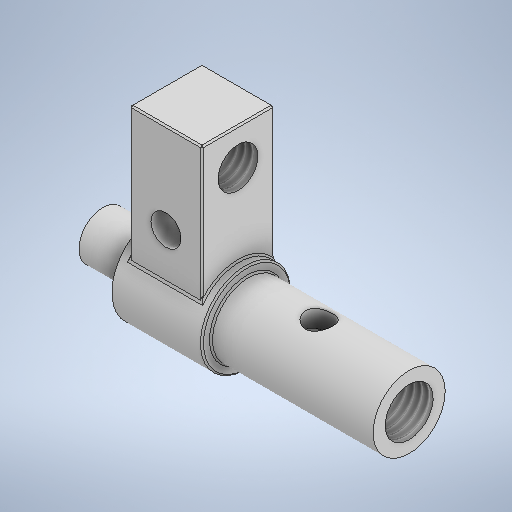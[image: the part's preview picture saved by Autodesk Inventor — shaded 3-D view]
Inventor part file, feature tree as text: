
AUTODESK INVENTOR PART (.ipt)
format: ipt  version: 2025.1 (Build 291241000, 241)  size: 380,928 bytes
history: native  units: mm
features: sketch x8, hole x6, plane x3, chamfer x3, revolve x1, extrude x1, thread x1
ambient origin geometry x8: Origin, YZ Plane, XZ Plane, XY Plane, X Axis, Y Axis, Z Axis, Center Point
bodies: Solid1 (feature_tree)
feature tree (23):
  revolve  "Revolution1"  [1 undecoded]
  plane  "Work Plane1"
  extrude  "Extrusion1"  Depth=8.0mm
  plane  "Work Plane2"
  hole  "Hole1"  [1 undecoded]
  hole  "Hole2"  [1 undecoded]
  hole  "Hole4"  [1 undecoded]
  thread  "Thread1"  [1 undecoded]
  hole  "Hole5"  [1 undecoded]
  plane  "Work Plane5"
  hole  "Hole6"  [1 undecoded]
  hole  "Hole3"  [1 undecoded]
  chamfer  "Chamfer1"  Distance=10.0mm
  chamfer  "Chamfer2"  [1 undecoded]
  chamfer  "Chamfer3"  Distance=7.5mm
  sketch  "Sketch1"  dims[d0=15.0mm d1=27.0mm]
  sketch  "Sketch2"  dims[d2=9.0mm d3=8.0mm]
  sketch  "Sketch3"  dims[d4=12.0mm d5=15.0mm]
  sketch  "Sketch4"  dims[d6=90.0deg d7=27.0mm]
  sketch  "Sketch5"  dims[d8=12.0mm d9=12.0mm d10=10.0mm d11=0.0mm]
  sketch  "Sketch6"  dims[d12=6.0mm d13=15.0mm]
  sketch  "Sketch8"  dims[d14=4.5mm d15=6.0mm d16=4.0mm d17=2.0mm d18=90.0deg d19=8.0mm d20=20.594885mm]
  sketch  "Sketch10"  dims[d21=6.647mm d22=8.0mm d23=4.0mm d24=2.0mm d25=90.0deg d26=8.0mm d27=0.0mm d28=6.0mm d29=5.0mm d30=8.0mm d31=4.0mm d32=2.0mm d33=90.0deg d34=8.0mm d35=0.0mm d36=9.0mm d37=6.5mm d38=6.0mm d39=8.0mm d40=10.0mm d41=90.0deg d42=8.0mm d43=0.0mm d44=10.0mm d45=0.0mm d47=4.5mm d48=6.0mm d49=8.0mm d50=10.0mm d51=90.0deg d52=8.0mm d53=0.0mm d55=-7.5mm d56=7.5mm d57=2.5mm d58=6.0mm d59=4.0mm d60=2.0mm d61=90.0deg d62=25.0mm d63=0.0mm d64=0.25mm d65=2.0mm d66=45.0deg d67=0.25mm d68=2.0mm d69=45.0deg d70=0.25mm d71=2.0mm d72=45.0deg]
note: 9 required parameter values undecoded (feature->parameter linkage not recoverable at this tier; creation-order binding heuristic only, values carry confidence <= 0.55)